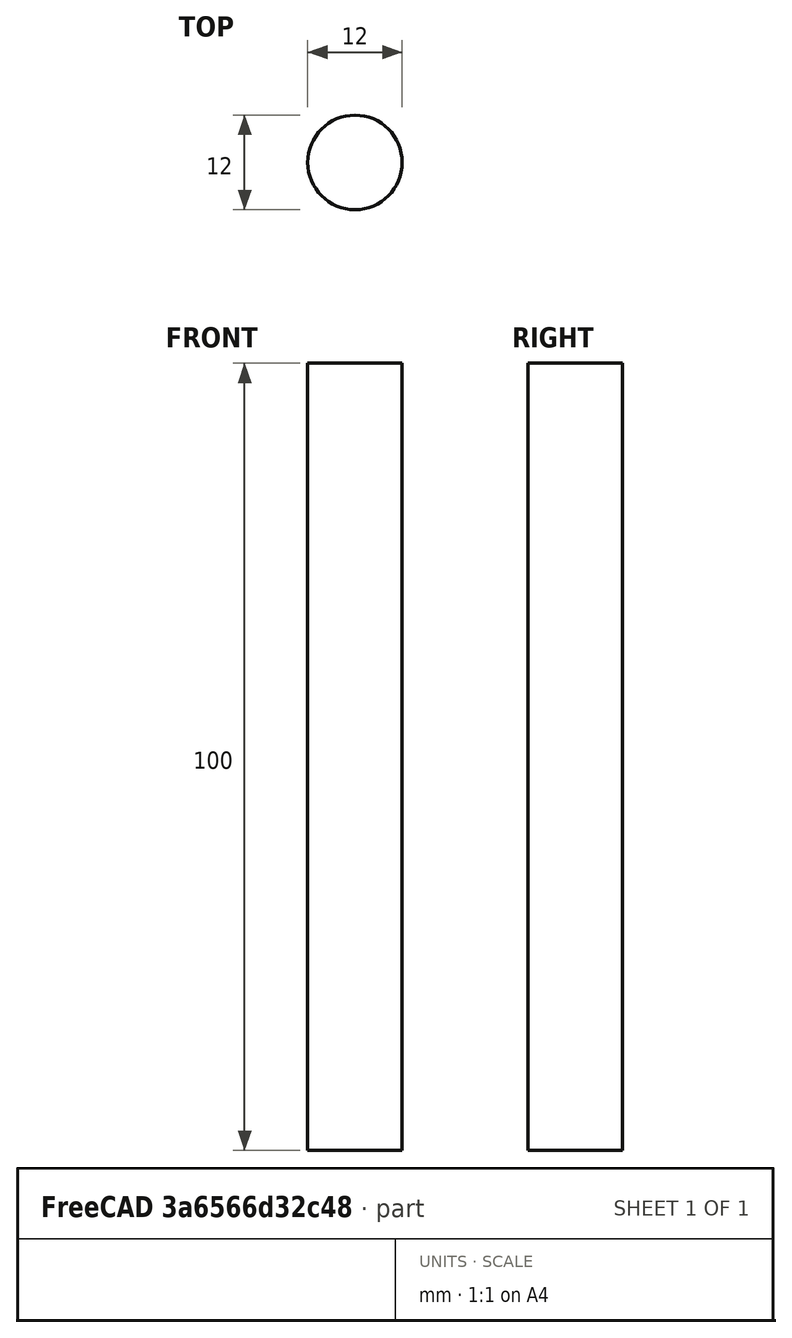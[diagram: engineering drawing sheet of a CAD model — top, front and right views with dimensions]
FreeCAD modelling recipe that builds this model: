
FCSTD DOCUMENT  (FreeCAD 1.0R39109 (Git))
Label: linear_slide
License: All rights reserved
LicenseURL: https://en.wikipedia.org/wiki/All_rights_reserved
objects: Sketcher::SketchObject×1, PartDesign::Pad×1, PartDesign::Body×1
note: 6 computed .brp shape members not serialized (recipe doc carries the construction recipe); baked Part::Feature solids carry a one-line shape summary decoded from their .brp

FEATURE [Sketcher::SketchObject] Sketch
  ArcFitTolerance = 1e-06
  AttachmentSupport = -> [XY_Plane]
  FullyConstrained = true
  MakeInternals = false
  MapMode = 5
  sketch-geometry (1):
    g0: Circle CenterX=0 CenterY=0 CenterZ=0 NormalX=0 NormalY=0 NormalZ=1 AngleXU=0 Radius=6
  constraints (2):
    c: Coincident(g0,g-1)
    c: Diameter(g0) = 12
FEATURE [PartDesign::Pad] Pad
  Direction = (0,0,1)
  Length = 100
  Length2 = 10
  Profile = -> Sketch
  ReferenceAxis = -> Sketch [N_Axis]
  Refine = true
  Suppressed = false
  Type = 0
FEATURE [PartDesign::Body] Body  label="linear_slide_12"
  AllowCompound = false
  Group = -> [Sketch,Pad]
  Origin = -> Origin
  Tip = -> Pad
